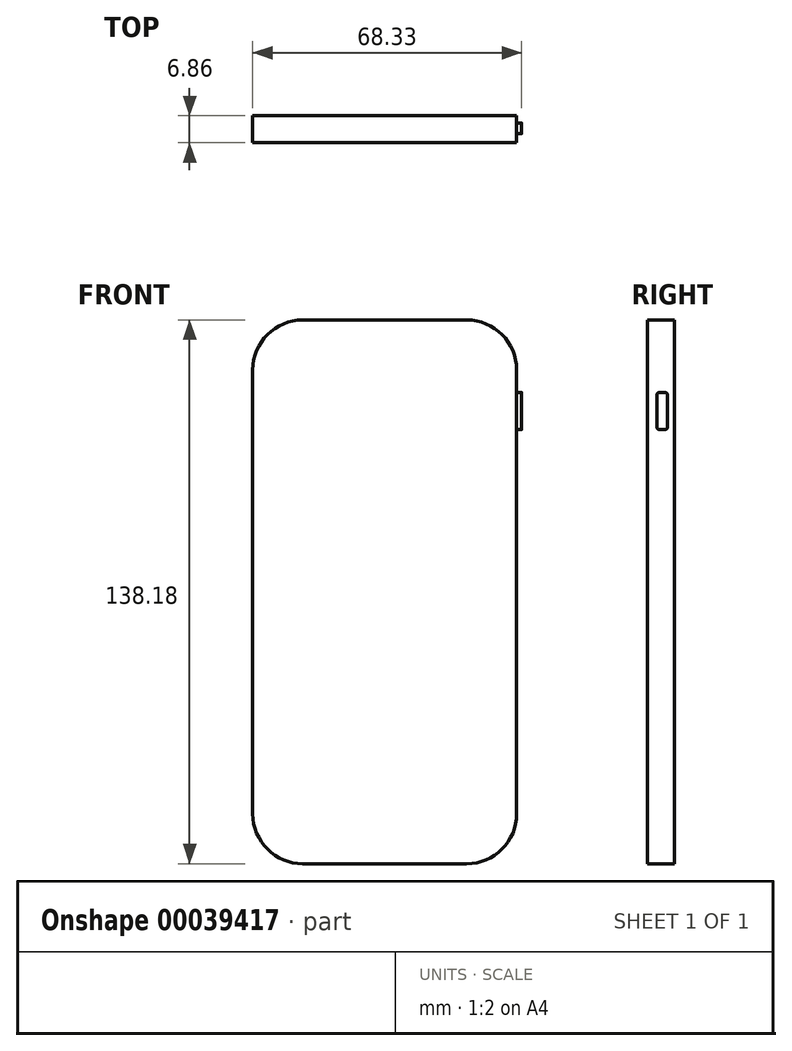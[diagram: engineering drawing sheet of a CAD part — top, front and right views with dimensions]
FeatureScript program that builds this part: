
annotation { "Feature Type Name" : "Feature", "Feature Type Description" : "" }
export const myFeature = defineFeature(function(context is Context, id is Id, definition is map)
    precondition{}
    {
        {
            var Q0;
            Q0=qCreatedBy(makeId("Front.planeOp"),FACE);
            var sketch = newSketch(context, id + "F0", { "sketchPlane" : qUnion([Q0])});
            skLineSegment(sketch, "E0", {"start": v(-67.06, 70.6) * mm, "end": v(-67.06, -67.57) * mm});
            skLineSegment(sketch, "E1", {"start": v(-67.06, -67.57) * mm, "end": v(0, -67.57) * mm});
            skLineSegment(sketch, "E2", {"start": v(0, -67.57) * mm, "end": v(0, 70.6) * mm});
            skLineSegment(sketch, "E3", {"start": v(0, 70.6) * mm, "end": v(-67.06, 70.6) * mm});
            skSolve(sketch);
        }
        {
            var Q0;
            Q0 = qSketchRegion(id + "F0", true);
            extrude(context, id + "F1", {"entities" : qUnion([Q0]), "depth" : 6.86 * mm});
        }
        {
            var Q0;
            Q0=makeQuery(id+"F1.opExtrude","SWEPT_EDGE",EDGE,{"disambiguationData":[OSD([sQuery(id+"F0.wireOp",EDGE,"E0"),sQuery(id+"F0.wireOp",EDGE,"E3")])]});
            fillet(context, id + "F2", {"entities" : qUnion([Q0]), "radius" : 12.7 * mm, "tangentPropagation" : true, "allowEdgeOverflow" : false});
        }
        {
            var Q0;
            Q0=makeQuery(id+"F1.opExtrude","SWEPT_EDGE",EDGE,{"disambiguationData":[OSD([sQuery(id+"F0.wireOp",EDGE,"E2"),sQuery(id+"F0.wireOp",EDGE,"E3")])]});
            fillet(context, id + "F3", {"entities" : qUnion([Q0]), "radius" : 12.7 * mm, "tangentPropagation" : true, "allowEdgeOverflow" : false});
        }
        {
            var Q0;
            Q0=makeQuery(id+"F1.opExtrude","SWEPT_EDGE",EDGE,{"disambiguationData":[OSD([sQuery(id+"F0.wireOp",EDGE,"E0"),sQuery(id+"F0.wireOp",EDGE,"E1")])]});
            fillet(context, id + "F4", {"entities" : qUnion([Q0]), "radius" : 12.7 * mm, "tangentPropagation" : true, "allowEdgeOverflow" : false});
        }
        {
            var Q0;
            Q0=makeQuery(id+"F1.opExtrude","SWEPT_EDGE",EDGE,{"disambiguationData":[OSD([sQuery(id+"F0.wireOp",EDGE,"E1"),sQuery(id+"F0.wireOp",EDGE,"E2")])]});
            fillet(context, id + "F5", {"entities" : qUnion([Q0]), "radius" : 12.7 * mm, "tangentPropagation" : true, "allowEdgeOverflow" : false});
        }
        {
            var Q0;
            Q0=makeQuery(id+"F1.opExtrude","CAP_FACE",FACE,{"disambiguationData":[OSD([sQuery(id+"F0.wireOp",EDGE,"E0"),sQuery(id+"F0.wireOp",EDGE,"E1"),sQuery(id+"F0.wireOp",EDGE,"E2"),sQuery(id+"F0.wireOp",EDGE,"E3")])],"isStart":false});
            var sketch = newSketch(context, id + "F6", { "sketchPlane" : qUnion([Q0])});
            skLineSegment(sketch, "E4", {"start": v(-63.88, 57.9) * mm, "end": v(-3.18, 57.9) * mm});
            skLineSegment(sketch, "E5", {"start": v(-3.18, 57.9) * mm, "end": v(-3.17, -54.87) * mm});
            skLineSegment(sketch, "E6", {"start": v(-3.17, -54.87) * mm, "end": v(-63.88, -54.87) * mm});
            skLineSegment(sketch, "E7", {"start": v(-63.88, -54.87) * mm, "end": v(-63.88, 57.9) * mm});
            skCircle(sketch, "E8", {"center": v(-33.74, -60.73) * mm, "radius": 4.25 * mm});
            skSolve(sketch);
        }
        {
            var Q0;
            Q0=sQuery(id+"F6.wireOp",EDGE,"E8");
            extrude(context, id + "F7", {"bodyType" : ToolBodyType.SURFACE, "surfaceEntities" : qUnion([Q0]), "oppositeDirection" : true, "depth" : 3.17 * mm});
        }
        {
            var Q0;
            Q0=makeQuery(id+"F1.opExtrude","SWEPT_FACE",FACE,{"disambiguationData":[OSD([sQuery(id+"F0.wireOp",EDGE,"E2")])]});
            var sketch = newSketch(context, id + "F8", { "sketchPlane" : qUnion([Q0])});
            skLineSegment(sketch, "E9", {"start": v(-4.54, 52.16) * mm, "end": v(-1.8, 52.16) * mm});
            skLineSegment(sketch, "E10", {"start": v(-1.8, 52.16) * mm, "end": v(-1.8, 42.75) * mm});
            skLineSegment(sketch, "E11", {"start": v(-1.8, 42.75) * mm, "end": v(-4.54, 42.75) * mm});
            skLineSegment(sketch, "E12", {"start": v(-4.54, 42.75) * mm, "end": v(-4.54, 52.16) * mm});
            skSolve(sketch);
        }
        {
            var Q0;
            Q0 = qSketchRegion(id + "F8", true);
            extrude(context, id + "F9", {"entities" : qUnion([Q0]), "operationType" : NewBodyOperationType.ADD, "depth" : 1.27 * mm});
        }
        {
            var Q0;
            Q0=makeQuery(id+"F9.opExtrude","SWEPT_EDGE",EDGE,{"disambiguationData":[OSD([sQuery(id+"F8.wireOp",EDGE,"E9"),sQuery(id+"F8.wireOp",EDGE,"E10")])]});
            fillet(context, id + "F10", {"entities" : qUnion([Q0]), "radius" : 0.64 * mm, "tangentPropagation" : true, "allowEdgeOverflow" : false});
        }
        {
            var Q0;
            Q0=makeQuery(id+"F9.opExtrude","SWEPT_EDGE",EDGE,{"disambiguationData":[OSD([sQuery(id+"F8.wireOp",EDGE,"E10"),sQuery(id+"F8.wireOp",EDGE,"E11")])]});
            fillet(context, id + "F11", {"entities" : qUnion([Q0]), "radius" : 0.64 * mm, "tangentPropagation" : true, "allowEdgeOverflow" : false});
        }
        {
            var Q0;
            Q0=makeQuery(id+"F9.opExtrude","SWEPT_EDGE",EDGE,{"disambiguationData":[OSD([sQuery(id+"F8.wireOp",EDGE,"E9"),sQuery(id+"F8.wireOp",EDGE,"E12")])]});
            fillet(context, id + "F12", {"entities" : qUnion([Q0]), "radius" : 0.64 * mm, "tangentPropagation" : true, "allowEdgeOverflow" : false});
        }
        {
            var Q0;
            Q0=makeQuery(id+"F9.opExtrude","SWEPT_EDGE",EDGE,{"disambiguationData":[OSD([sQuery(id+"F8.wireOp",EDGE,"E11"),sQuery(id+"F8.wireOp",EDGE,"E12")])]});
            fillet(context, id + "F13", {"entities" : qUnion([Q0]), "radius" : 0.64 * mm, "tangentPropagation" : true, "allowEdgeOverflow" : false});
        }
    });
